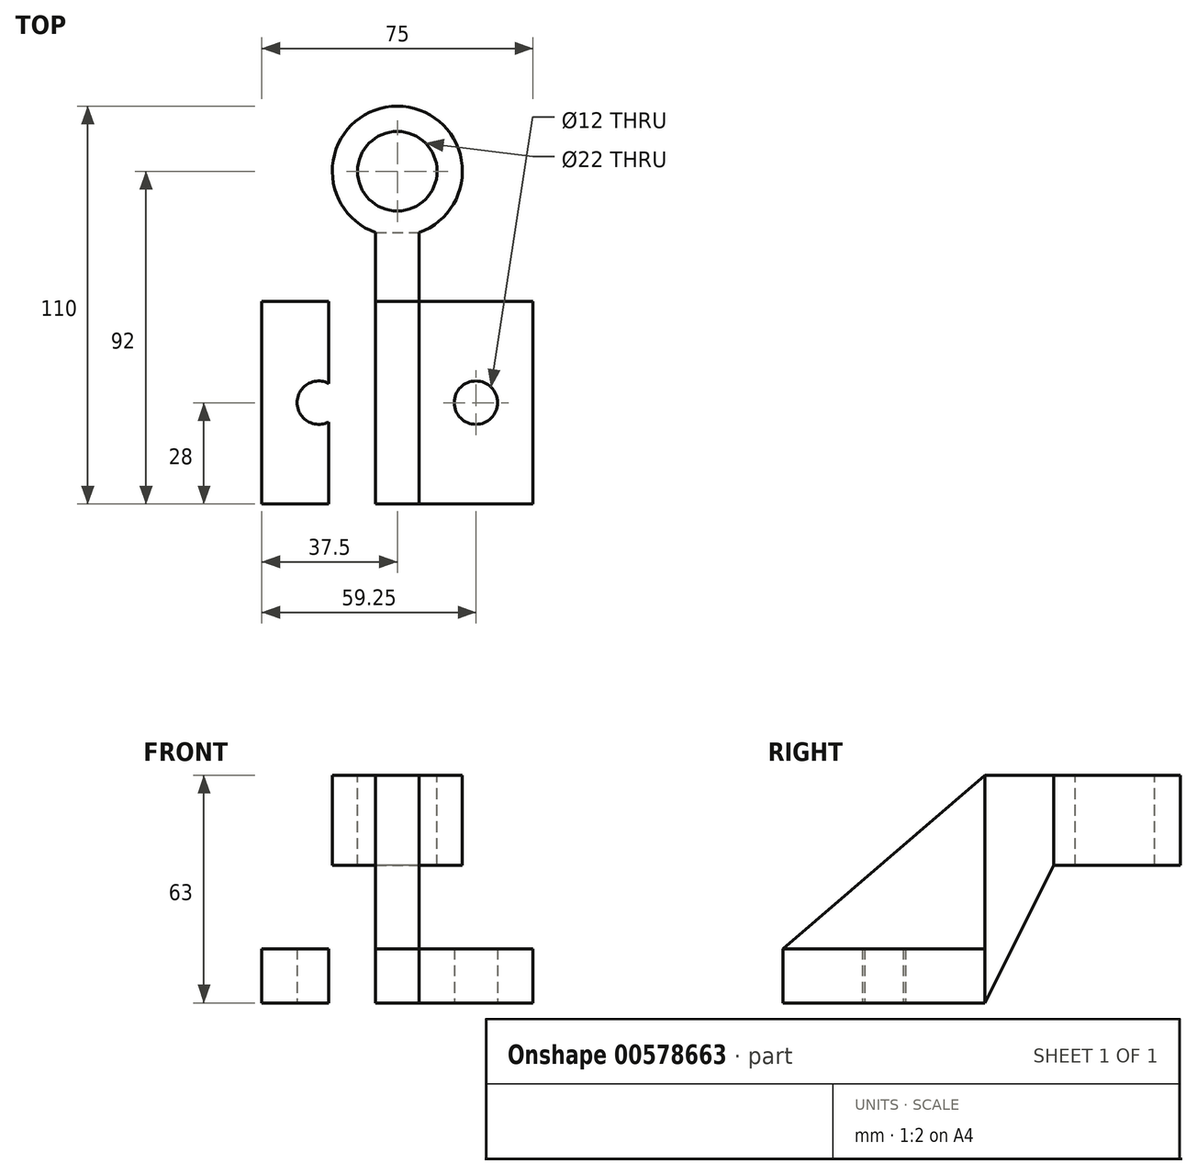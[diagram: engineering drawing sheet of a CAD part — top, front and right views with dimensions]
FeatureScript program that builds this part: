
annotation { "Feature Type Name" : "Feature", "Feature Type Description" : "" }
export const myFeature = defineFeature(function(context is Context, id is Id, definition is map)
    precondition{}
    {
        {
            var Q0;
            Q0=qCreatedBy(makeId("Top.planeOp"),FACE);
            var sketch = newSketch(context, id + "F0", { "sketchPlane" : qUnion([Q0])});
            skLineSegment(sketch, "E0.bottom", {"start": v(37.5, 28) * mm, "end": v(-37.5, 28) * mm});
            skLineSegment(sketch, "E0.top", {"start": v(37.5, -28) * mm, "end": v(-37.5, -28) * mm});
            skLineSegment(sketch, "E0.left", {"start": v(37.5, 28) * mm, "end": v(37.5, -28) * mm});
            skLineSegment(sketch, "E0.right", {"start": v(-37.5, 28) * mm, "end": v(-37.5, -28) * mm});
            skPoint(sketch, "E0.middle", {"position": v(0, 0) * mm});
            skLineSegment(sketch, "E1", {"start": v(0, 28) * mm, "end": v(0, -28) * mm});
            skLineSegment(sketch, "E2", {"start": v(-6, -28) * mm, "end": v(-6, 28) * mm});
            skLineSegment(sketch, "E3", {"start": v(6, -28) * mm, "end": v(6, 28) * mm});
            skLineSegment(sketch, "E4", {"start": v(-6, 28) * mm, "end": v(-37.5, 28) * mm});
            skLineSegment(sketch, "E5", {"start": v(6, 28) * mm, "end": v(37.5, 28) * mm});
            skCircle(sketch, "E6", {"center": v(-21.75, 0) * mm, "radius": 6 * mm});
            skPoint(sketch, "E6.centerSnap0", {"position": v(-21.75, 28) * mm});
            skCircle(sketch, "E7", {"center": v(21.75, 0) * mm, "radius": 6 * mm});
            skPoint(sketch, "E7.centerSnap0", {"position": v(21.75, 28) * mm});
            skSolve(sketch);
        }
        {
            var Q0;
            {var subQ1=sQuery(id+"F0.wireOp",EDGE,"E0.right");Q0=makeQuery(id+"F0.imprint","IMPRINT",FACE,{"disambiguationData":[TD([[makeQuery(id+"F0.imprint","IMPRINT",EDGE,{"derivedFrom":subQ1}),1.0]])]});}
            var Q1;
            {var subQ1=sQuery(id+"F0.wireOp",EDGE,"E0.left");Q1=makeQuery(id+"F0.imprint","IMPRINT",FACE,{"disambiguationData":[TD([[makeQuery(id+"F0.imprint","IMPRINT",EDGE,{"derivedFrom":subQ1}),-1.0]])]});}
            extrude(context, id + "F1", {"entities" : qUnion([Q0, Q1]), "depth" : 15 * mm, "offsetDistance" : 25 * mm});
        }
        {
            var Q0;
            {var subQ2=sQuery(id+"F0.wireOp",EDGE,"E1");Q0=makeQuery(id+"F0.imprint","IMPRINT",FACE,{"disambiguationData":[TD([[makeQuery(id+"F0.imprint","IMPRINT",EDGE,{"derivedFrom":subQ2}),-1.0]])]});}
            var Q1;
            {var subQ2=sQuery(id+"F0.wireOp",EDGE,"E1");Q1=makeQuery(id+"F0.imprint","IMPRINT",FACE,{"disambiguationData":[TD([[makeQuery(id+"F0.imprint","IMPRINT",EDGE,{"derivedFrom":subQ2}),1.0]])]});}
            extrude(context, id + "F2", {"entities" : qUnion([Q0, Q1]), "depth" : 63 * mm, "offsetDistance" : 25 * mm});
        }
        {
            var Q0;
            Q0=makeQuery(id+"F2.opExtrude","SWEPT_FACE",FACE,{"disambiguationData":[OSD([sQuery(id+"F0.wireOp",EDGE,"E3")])]});
            var sketch = newSketch(context, id + "F3", { "sketchPlane" : qUnion([Q0])});
            skLineSegment(sketch, "E8.0.0", {"start": v(-28, 0) * mm, "end": v(28, 0) * mm});
            skLineSegment(sketch, "E8.0.1", {"start": v(28, 0) * mm, "end": v(28, 63) * mm});
            skLineSegment(sketch, "E8.0.2", {"start": v(28, 63) * mm, "end": v(-28, 63) * mm});
            skLineSegment(sketch, "E8.0.3", {"start": v(-28, 63) * mm, "end": v(-28, 0) * mm});
            skLineSegment(sketch, "E9.0", {"start": v(28, 15) * mm, "end": v(-28, 15) * mm});
            skLineSegment(sketch, "E10", {"start": v(28, 63) * mm, "end": v(-28, 15) * mm});
            skSolve(sketch);
        }
        {
            var Q0;
            {var subQ0=sQuery(id+"F3.wireOp",EDGE,"E8.0.2");Q0=makeQuery(id+"F3.imprint","IMPRINT",FACE,{"disambiguationData":[TD([[makeQuery(id+"F3.imprint","IMPRINT",EDGE,{"derivedFrom":subQ0}),-1.0]])]});}
            extrude(context, id + "F4", {"entities" : qUnion([Q0]), "operationType" : NewBodyOperationType.REMOVE, "oppositeDirection" : true, "depth" : 25 * mm, "offsetDistance" : 25 * mm});
        }
        {
            var Q0;
            Q0=makeQuery(id+"F2.opExtrude","SWEPT_FACE",FACE,{"disambiguationData":[OSD([sQuery(id+"F0.wireOp",EDGE,"E0.bottom")])]});
            var sketch = newSketch(context, id + "F5", { "sketchPlane" : qUnion([Q0])});
            skSolve(sketch);
        }
        {
            var Q0;
            Q0 = qSketchRegion(id + "F5", true);
            var Q1;
            {var subQ0=sQuery(id+"F0.wireOp",EDGE,"E0.bottom");Q1=makeQuery(id+"F5.imprint","IMPRINT",FACE,{"disambiguationData":[TD([[makeQuery(id+"F5.imprint","IMPRINT",EDGE,{"derivedFrom":makeQuery(id+"F2.opExtrude","CAP_EDGE",EDGE,{"disambiguationData":[OSD([subQ0])],"isStart":true})}),1.0]])]});}
            extrude(context, id + "F6", {"entities" : qUnion([Q0, Q1]), "depth" : 36 * mm, "offsetDistance" : 25 * mm});
        }
        {
            var Q0;
            Q0=makeQuery(id+"F6.opExtrude","SWEPT_FACE",FACE,{"disambiguationData":[OSD([sQuery(id+"F0.wireOp",EDGE,"E0.bottom"),sQuery(id+"F3.wireOp",EDGE,"E8.0.1"),sQuery(id+"F3.wireOp",EDGE,"E8.0.2"),sQuery(id+"F3.wireOp",EDGE,"E10")])]});
            var sketch = newSketch(context, id + "F7", { "sketchPlane" : qUnion([Q0])});
            skCircle(sketch, "E11", {"center": v(0, 64) * mm, "radius": 11 * mm});
            skCircle(sketch, "E12", {"center": v(0, 64) * mm, "radius": 18 * mm});
            skSolve(sketch);
        }
        {
            var Q0;
            {var subQ1=sQuery(id+"F3.wireOp",EDGE,"E10");var subQ2=sQuery(id+"F3.wireOp",EDGE,"E8.0.2");var subQ3=sQuery(id+"F3.wireOp",EDGE,"E8.0.1");var subQ4=sQuery(id+"F0.wireOp",EDGE,"E0.bottom");var subQ9=makeQuery(id+"F6.opExtrude","CAP_EDGE",EDGE,{"disambiguationData":[OSD([subQ4,subQ3,subQ2,subQ1])],"isStart":false});Q0=makeQuery(id+"F7.imprint","IMPRINT",FACE,{"disambiguationData":[TD([[makeQuery(id+"F7.imprint","IMPRINT",EDGE,{"derivedFrom":subQ9}),1.0]])]});}
            extrude(context, id + "F8", {"entities" : qUnion([Q0]), "operationType" : NewBodyOperationType.REMOVE, "oppositeDirection" : true, "depth" : 212.8 * mm, "offsetDistance" : 25 * mm});
        }
        {
            var Q0;
            {var subQ0=sQuery(id+"F7.wireOp",EDGE,"E11");var subQ1=sQuery(id+"F3.wireOp",EDGE,"E10");var subQ2=sQuery(id+"F3.wireOp",EDGE,"E8.0.2");var subQ3=sQuery(id+"F3.wireOp",EDGE,"E8.0.1");var subQ4=sQuery(id+"F0.wireOp",EDGE,"E0.bottom");var subQ5=makeQuery(id+"F6.opExtrude","SWEPT_EDGE",EDGE,{"disambiguationData":[OSD([subQ4,sQuery(id+"F0.wireOp",EDGE,"E3"),sQuery(id+"F0.wireOp",EDGE,"E5"),subQ3,subQ2,subQ1])]});var subQ6=makeQuery(id+"F7.imprint","INTERSECT",VERTEX,{"derivedFrom":[subQ5,subQ0]});Q0=makeQuery(id+"F7.imprint","IMPRINT",FACE,{"disambiguationData":[TD([[makeQuery(id+"F7.imprint","IMPRINT",EDGE,{"disambiguationData":[TD([[subQ6,-1.0]])],"derivedFrom":subQ0}),-1.0]])]});}
            extrude(context, id + "F9", {"entities" : qUnion([Q0]), "operationType" : NewBodyOperationType.ADD, "oppositeDirection" : true, "depth" : 25 * mm, "offsetDistance" : 25 * mm});
        }
        {
            var Q0;
            Q0=makeQuery(id+"F6.opExtrude","SWEPT_FACE",FACE,{"disambiguationData":[OSD([sQuery(id+"F0.wireOp",EDGE,"E0.bottom"),sQuery(id+"F0.wireOp",EDGE,"E3"),sQuery(id+"F0.wireOp",EDGE,"E5")])]});
            var sketch = newSketch(context, id + "F10", { "sketchPlane" : qUnion([Q0])});
            skPoint(sketch, "E13.0", {"position": v(28, 31.5) * mm});
            skLineSegment(sketch, "E14.0", {"start": v(28, 63) * mm, "end": v(28, 0) * mm});
            skLineSegment(sketch, "E15.0.0", {"start": v(-28, 0) * mm, "end": v(28, 0) * mm});
            skLineSegment(sketch, "E15.0.1", {"start": v(28, 0) * mm, "end": v(28, 15) * mm});
            skLineSegment(sketch, "E15.0.2", {"start": v(28, 15) * mm, "end": v(-28, 15) * mm});
            skLineSegment(sketch, "E15.0.3", {"start": v(-28, 15) * mm, "end": v(-28, 0) * mm});
            skLineSegment(sketch, "E16", {"start": v(47.03, 38) * mm, "end": v(28, 0) * mm});
            skSolve(sketch);
        }
        {
            var Q0;
            Q0 = qSketchRegion(id + "F10", true);
            extrude(context, id + "F11", {"entities" : qUnion([Q0]), "operationType" : NewBodyOperationType.REMOVE, "oppositeDirection" : true, "depth" : 25 * mm, "offsetDistance" : 25 * mm});
        }
        {
            var Q0;
            Q0=makeQuery(id+"F10.imprint","IMPRINT",FACE,{"disambiguationData":[TD([[makeQuery(id+"F10.imprint","IMPRINT",EDGE,{"derivedFrom":sQuery(id+"F10.wireOp",EDGE,"E16")}),1.0]])]});
            extrude(context, id + "F12", {"entities" : qUnion([Q0]), "operationType" : NewBodyOperationType.REMOVE, "oppositeDirection" : true, "depth" : 25 * mm, "offsetDistance" : 25 * mm});
        }
    });
